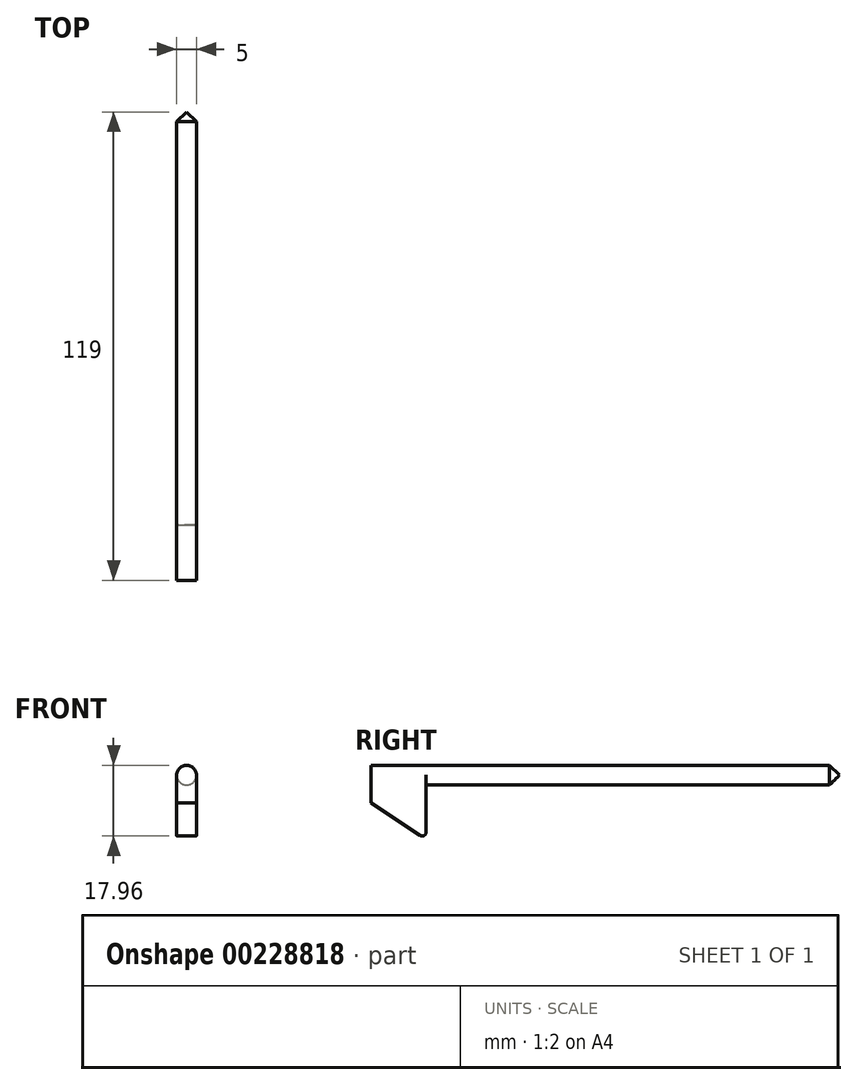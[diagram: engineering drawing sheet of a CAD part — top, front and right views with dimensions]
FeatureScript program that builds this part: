
annotation { "Feature Type Name" : "Feature", "Feature Type Description" : "" }
export const myFeature = defineFeature(function(context is Context, id is Id, definition is map)
    precondition{}
    {
        {
            var Q0;
            Q0=qCreatedBy(makeId("Front.planeOp"),FACE);
            var sketch = newSketch(context, id + "F0", { "sketchPlane" : qUnion([Q0])});
            skCircle(sketch, "E0", {"center": v(0, 0) * mm, "radius": 2.5 * mm});
            skSolve(sketch);
        }
        {
            var Q0;
            Q0=makeQuery(id+"F0.imprint","IMPRINT",FACE,{"disambiguationData":[TD([[makeQuery(id+"F0.imprint","IMPRINT",EDGE,{"derivedFrom":sQuery(id+"F0.wireOp",EDGE,"E0")}),1.0]])]});
            extrude(context, id + "F1", {"entities" : qUnion([Q0]), "oppositeDirection" : true, "depth" : 105 * mm});
        }
        {
            var Q0;
            Q0=makeQuery(id+"F1.opExtrude","CAP_FACE",FACE,{"disambiguationData":[OSD([sQuery(id+"F0.wireOp",EDGE,"E0")])],"isStart":true});
            var sketch = newSketch(context, id + "F2", { "sketchPlane" : qUnion([Q0])});
            skLineSegment(sketch, "E1.bottom", {"start": v(-2.5, 0) * mm, "end": v(2.5, 0) * mm, "construction": true});
            skLineSegment(sketch, "E1.top", {"start": v(-2.5, -17) * mm, "end": v(2.5, -17) * mm});
            skLineSegment(sketch, "E1.left", {"start": v(2.5, 0) * mm, "end": v(2.5, -17) * mm});
            skLineSegment(sketch, "E1.right", {"start": v(-2.5, 0) * mm, "end": v(-2.5, -17) * mm});
            skCircle(sketch, "E2", {"center": v(0, 0) * mm, "radius": 2.5 * mm});
            skSolve(sketch);
        }
        {
            var Q0;
            Q0 = qSketchRegion(id + "F2", true);
            extrude(context, id + "F3", {"entities" : qUnion([Q0]), "operationType" : NewBodyOperationType.ADD, "depth" : 14 * mm});
        }
        {
            var Q0;
            Q0=makeQuery(id+"F1.opExtrude","CAP_EDGE",EDGE,{"disambiguationData":[OSD([sQuery(id+"F0.wireOp",EDGE,"E0")])],"isStart":false});
            chamfer(context, id + "F4", {"entities" : qUnion([Q0]), "width" : 2.5 * mm, "tangentPropagation" : true});
        }
        {
            var Q0;
            Q0=makeQuery(id+"F3.opExtrude","CAP_EDGE",EDGE,{"disambiguationData":[OSD([sQuery(id+"F2.wireOp",EDGE,"E1.top")])],"isStart":false});
            chamfer(context, id + "F5", {"entities" : qUnion([Q0]), "chamferType" : ChamferType.TWO_OFFSETS, "width1" : 10 * mm, "oppositeDirection" : false, "width2" : 15 * mm, "tangentPropagation" : true});
        }
        {
            var Q0;
            {var subQ0=sQuery(id+"F2.wireOp",EDGE,"E1.top");Q0=makeQuery(id+"F5.opChamfer","BLEND_EDGE",EDGE,{"blendedFrom":[makeQuery(id+"F3.opExtrude","CAP_EDGE",EDGE,{"disambiguationData":[OSD([subQ0])],"isStart":false}),makeQuery(id+"F3.opExtrude","CAP_FACE",FACE,{"disambiguationData":[OSD([subQ0,sQuery(id+"F2.wireOp",EDGE,"E1.left"),sQuery(id+"F2.wireOp",EDGE,"E1.right"),sQuery(id+"F2.wireOp",EDGE,"E2")])],"isStart":true})],"blendedInto":[makeQuery(id+"F3.opExtrude","CAP_FACE",FACE,{"disambiguationData":[OSD([subQ0,sQuery(id+"F2.wireOp",EDGE,"E1.left"),sQuery(id+"F2.wireOp",EDGE,"E1.right"),sQuery(id+"F2.wireOp",EDGE,"E2")])],"isStart":true})]});}
            fillet(context, id + "F6", {"entities" : qUnion([Q0]), "radius" : 1 * mm, "tangentPropagation" : true, "allowEdgeOverflow" : false});
        }
    });
